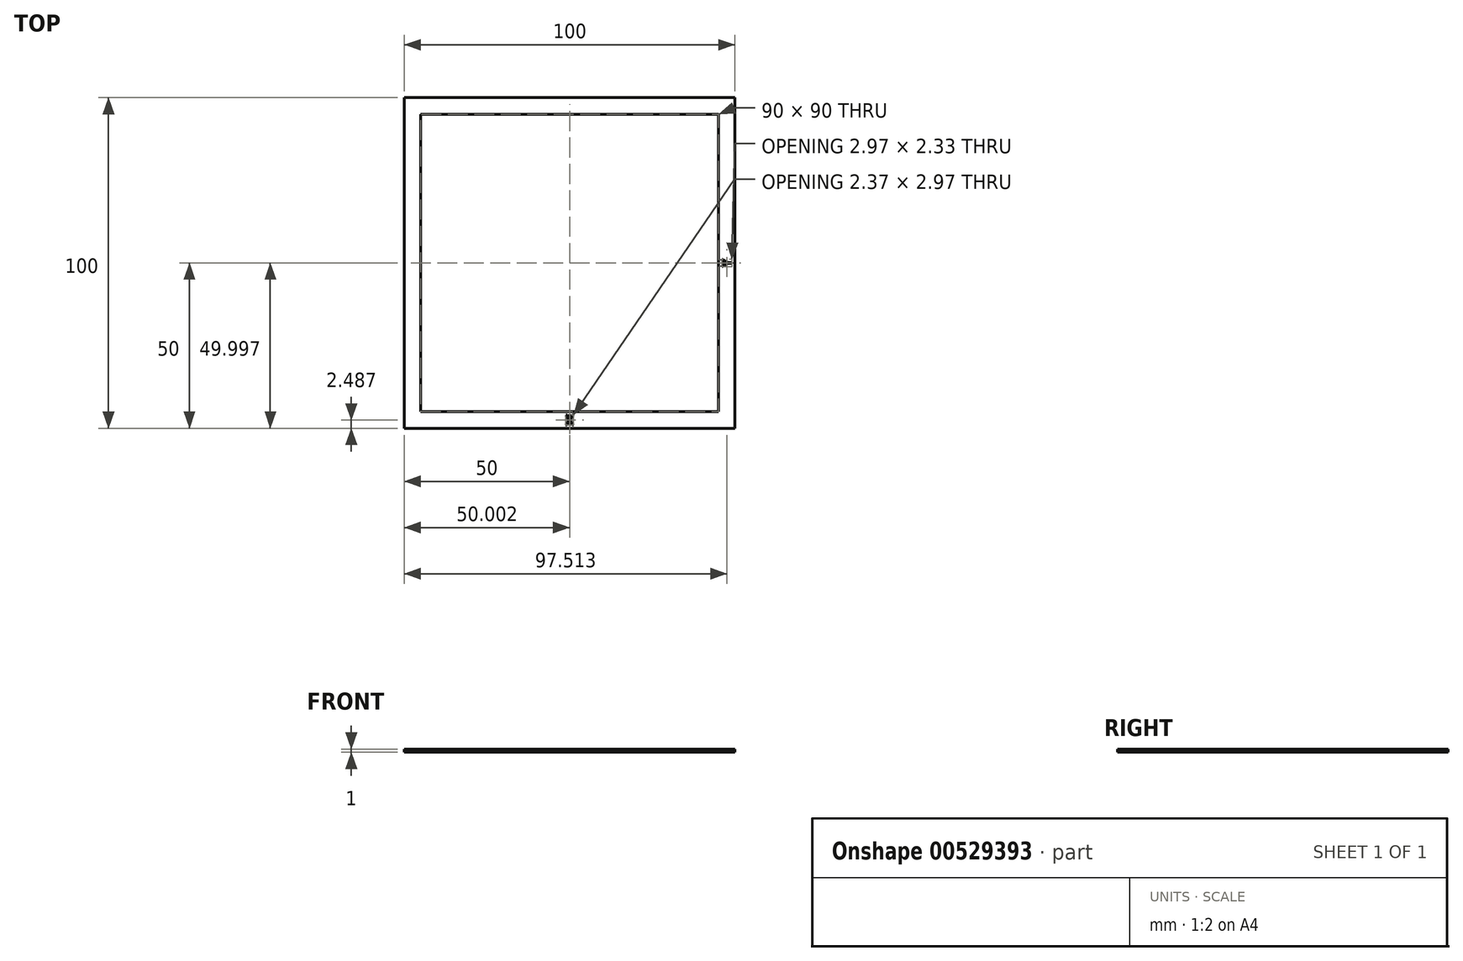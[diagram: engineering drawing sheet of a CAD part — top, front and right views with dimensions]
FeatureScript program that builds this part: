
annotation { "Feature Type Name" : "Feature", "Feature Type Description" : "" }
export const myFeature = defineFeature(function(context is Context, id is Id, definition is map)
    precondition{}
    {
        {
            var Q0;
            Q0=qCreatedBy(makeId("Top.planeOp"),FACE);
            var sketch = newSketch(context, id + "F0", { "sketchPlane" : qUnion([Q0])});
            skLineSegment(sketch, "E0.bottom", {"start": v(0, 0) * mm, "end": v(100, 0) * mm});
            skLineSegment(sketch, "E0.top", {"start": v(0, 100) * mm, "end": v(100, 100) * mm});
            skLineSegment(sketch, "E0.left", {"start": v(0, 0) * mm, "end": v(0, 100) * mm});
            skLineSegment(sketch, "E0.right", {"start": v(100, 0) * mm, "end": v(100, 100) * mm});
            skLineSegment(sketch, "E1.bottom", {"start": v(95, 95) * mm, "end": v(5, 95) * mm});
            skLineSegment(sketch, "E1.top", {"start": v(95, 5) * mm, "end": v(5, 5) * mm});
            skLineSegment(sketch, "E1.left", {"start": v(95, 95) * mm, "end": v(95, 5) * mm});
            skLineSegment(sketch, "E1.right", {"start": v(5, 95) * mm, "end": v(5, 5) * mm});
            skPoint(sketch, "E1.middle", {"position": v(50, 50) * mm});
            skPoint(sketch, "E1.middle.positionSnap0", {"position": v(50, 100) * mm});
            skPoint(sketch, "E1.centerSnap0", {"position": v(50, 100) * mm});
            skSolve(sketch);
        }
        {
            var Q0;
            Q0 = qSketchRegion(id + "F0", true);
            extrude(context, id + "F1", {"entities" : qUnion([Q0]), "depth" : 1 * mm, "offsetDistance" : 25 * mm});
        }
        {
            var Q0;
            Q0=makeQuery(id+"F1.opExtrude","CAP_FACE",FACE,{"disambiguationData":[OSD([sQuery(id+"F0.wireOp",EDGE,"E0.bottom"),sQuery(id+"F0.wireOp",EDGE,"E0.top"),sQuery(id+"F0.wireOp",EDGE,"E0.left"),sQuery(id+"F0.wireOp",EDGE,"E0.right"),sQuery(id+"F0.wireOp",EDGE,"E1.bottom"),sQuery(id+"F0.wireOp",EDGE,"E1.top"),sQuery(id+"F0.wireOp",EDGE,"E1.left"),sQuery(id+"F0.wireOp",EDGE,"E1.right")])],"isStart":false});
            var sketch = newSketch(context, id + "F2", { "sketchPlane" : qUnion([Q0])});
            skText(sketch, "E2", { "text": "X", "fontName": "OpenSans-Regular.ttf"});
            skLineSegment(sketch, "E3", {"start": v(50, 2.3) * mm, "end": v(50.13, 2.3) * mm, "construction": true});
            skText(sketch, "E4", { "text": "Y", "fontName": "OpenSans-Regular.ttf"});
            skLineSegment(sketch, "E5", {"start": v(97.5, 50.14) * mm, "end": v(97.5, 50) * mm, "construction": true});
            const initialGuessF2  = {"E2": [0.0488, 0.001, 1, 0, 0.003], "E4": [0.099, 0.04883, 0, 1, 0.003]};
            skSetInitialGuess(sketch, initialGuessF2);
            skSolve(sketch);
        }
        {
            var Q0;
            Q0 = qSketchRegion(id + "F2", true);
            extrude(context, id + "F3", {"entities" : qUnion([Q0]), "operationType" : NewBodyOperationType.REMOVE, "endBound" : BoundingType.THROUGH_ALL, "oppositeDirection" : true, "depth" : 25 * mm, "offsetDistance" : 25 * mm});
        }
    });
